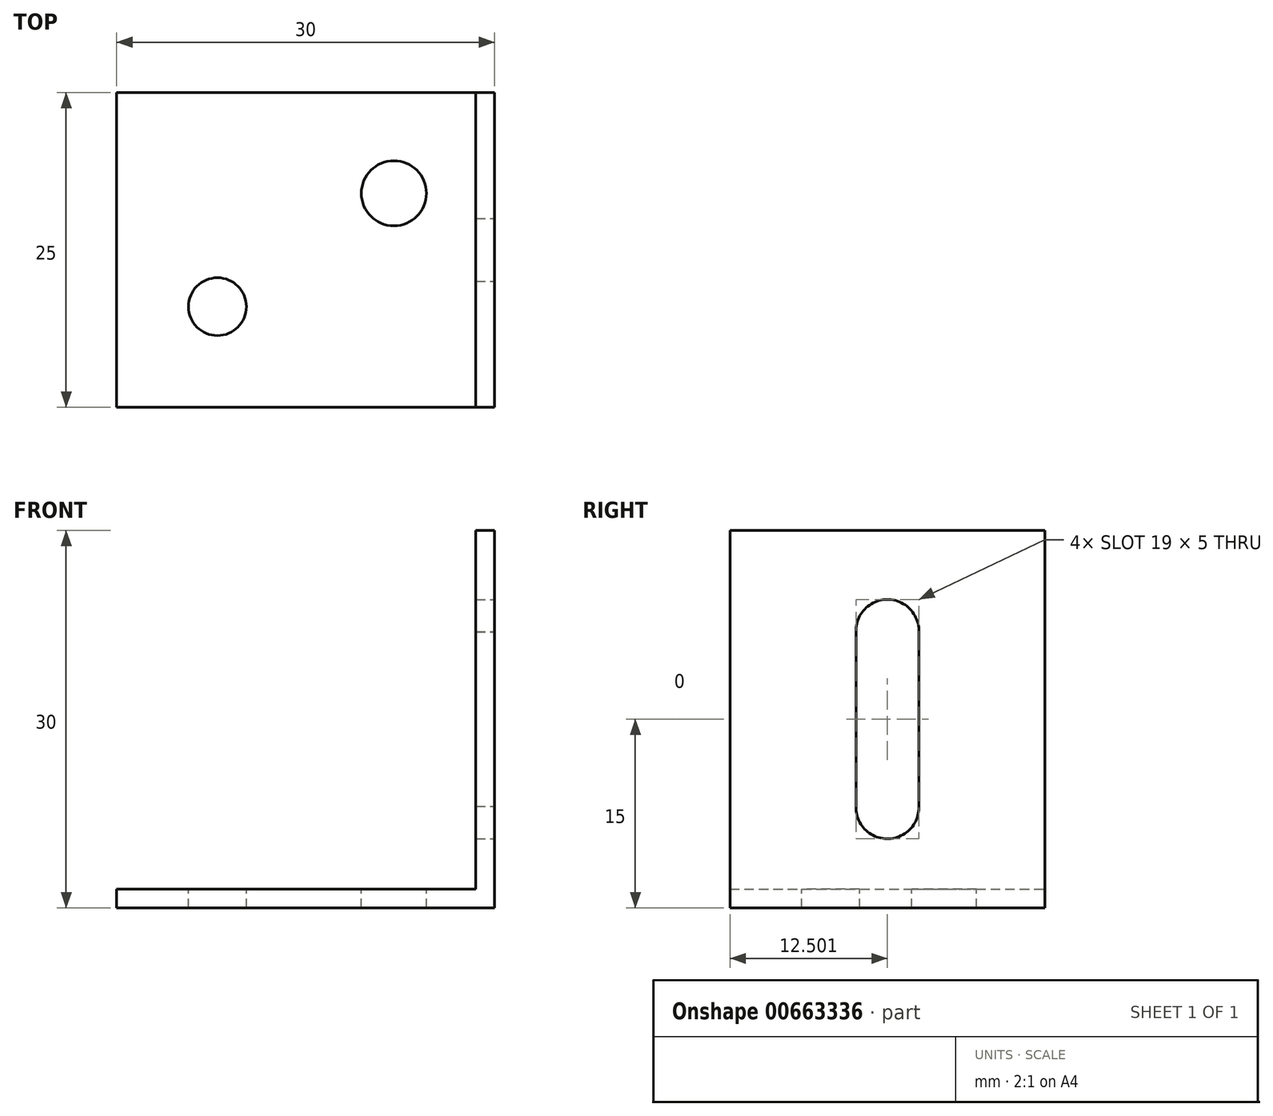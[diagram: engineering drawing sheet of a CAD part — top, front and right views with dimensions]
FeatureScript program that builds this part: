
annotation { "Feature Type Name" : "Feature", "Feature Type Description" : "" }
export const myFeature = defineFeature(function(context is Context, id is Id, definition is map)
    precondition{}
    {
        {
            var Q0;
            Q0=qCreatedBy(makeId("Front.planeOp"),FACE);
            var sketch = newSketch(context, id + "F0", { "sketchPlane" : qUnion([Q0])});
            skLineSegment(sketch, "E0", {"start": v(0, 30) * mm, "end": v(0, 0) * mm});
            skLineSegment(sketch, "E1", {"start": v(0, 0) * mm, "end": v(-30, 0) * mm});
            skLineSegment(sketch, "E2", {"start": v(-30, 0) * mm, "end": v(-30, 1.5) * mm});
            skLineSegment(sketch, "E3", {"start": v(-30, 1.5) * mm, "end": v(-1.5, 1.5) * mm});
            skLineSegment(sketch, "E4", {"start": v(-1.5, 1.5) * mm, "end": v(-1.5, 30) * mm});
            skLineSegment(sketch, "E5", {"start": v(-1.5, 30) * mm, "end": v(0, 30) * mm});
            skSolve(sketch);
        }
        {
            var Q0;
            Q0 = qSketchRegion(id + "F0", true);
            extrude(context, id + "F1", {"entities" : qUnion([Q0]), "depth" : 25 * mm, "offsetDistance" : 25 * mm});
        }
        {
            var Q0;
            Q0=makeQuery(id+"F1.opExtrude","SWEPT_FACE",FACE,{"disambiguationData":[OSD([sQuery(id+"F0.wireOp",EDGE,"E3")])]});
            var sketch = newSketch(context, id + "F2", { "sketchPlane" : qUnion([Q0])});
            skCircle(sketch, "E6", {"center": v(-22, -17) * mm, "radius": 2.3 * mm});
            skCircle(sketch, "E7", {"center": v(-8, -8) * mm, "radius": 2.58 * mm});
            skSolve(sketch);
        }
        {
            var Q0;
            Q0 = qSketchRegion(id + "F2", true);
            extrude(context, id + "F3", {"entities" : qUnion([Q0]), "operationType" : NewBodyOperationType.REMOVE, "oppositeDirection" : true, "depth" : 25 * mm, "offsetDistance" : 25 * mm});
        }
        {
            var Q0;
            Q0=makeQuery(id+"F1.opExtrude","SWEPT_FACE",FACE,{"disambiguationData":[OSD([sQuery(id+"F0.wireOp",EDGE,"E0")])]});
            var sketch = newSketch(context, id + "F4", { "sketchPlane" : qUnion([Q0])});
            skLineSegment(sketch, "E8", {"start": v(-12.5, 34.55) * mm, "end": v(-12.5, -8.13) * mm, "construction": true});
            skArc(sketch, "E9", {"start": v(-10, 21.94) * mm, "mid": v(-12.5, 24.5) * mm, "end": v(-15, 21.93) * mm});
            skArc(sketch, "E10", {"start": v(-15, 8.07) * mm, "mid": v(-12.54, 5.5) * mm, "end": v(-10, 8) * mm});
            skLineSegment(sketch, "E11", {"start": v(-15, 22.07) * mm, "end": v(-15, 7.93) * mm});
            skLineSegment(sketch, "E12", {"start": v(-10, 22.06) * mm, "end": v(-10, 8) * mm});
            skSolve(sketch);
        }
        {
            var Q0;
            Q0 = qSketchRegion(id + "F4", true);
            extrude(context, id + "F5", {"entities" : qUnion([Q0]), "operationType" : NewBodyOperationType.REMOVE, "oppositeDirection" : true, "depth" : 25 * mm, "offsetDistance" : 25 * mm});
        }
    });
